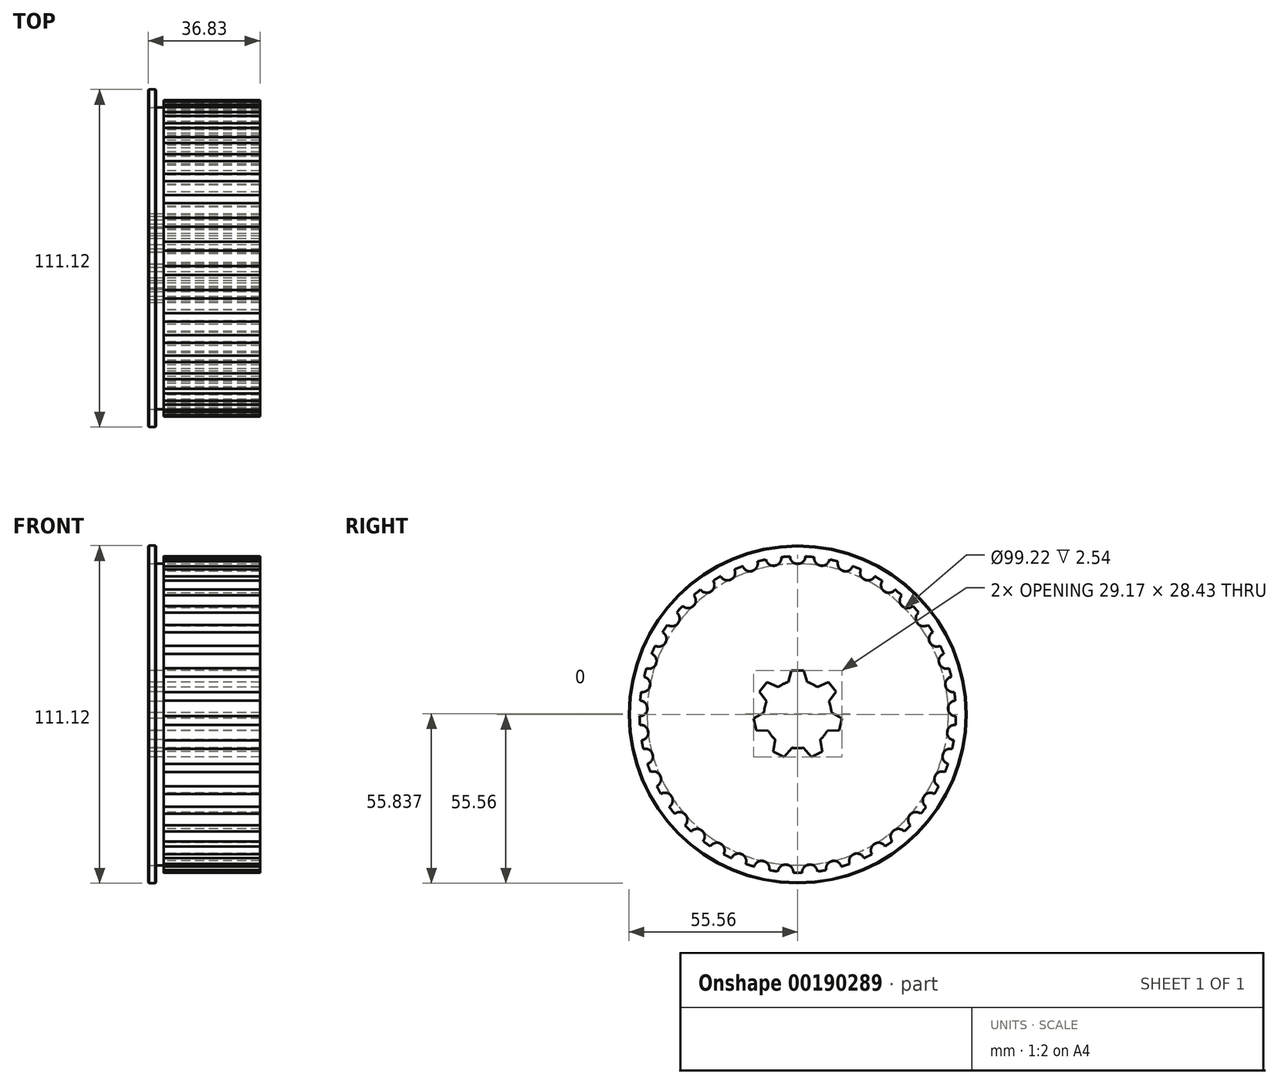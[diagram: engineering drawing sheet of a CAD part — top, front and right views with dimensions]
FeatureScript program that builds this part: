
annotation { "Feature Type Name" : "Feature", "Feature Type Description" : "" }
export const myFeature = defineFeature(function(context is Context, id is Id, definition is map)
    precondition{}
    {
        {
            var Q0;
            Q0=qCreatedBy(makeId("Right.planeOp"),FACE);
            var sketch = newSketch(context, id + "F9", { "sketchPlane" : qUnion([Q0])});
            skArc(sketch, "E0", {"start": v(-2.54, 52) * mm, "mid": v(0, -52.07) * mm, "end": v(2.54, 52) * mm});
            skArc(sketch, "E1", {"start": v(-2.54, 52) * mm, "mid": v(0, 49.53) * mm, "end": v(2.54, 52) * mm});
            skArc(sketch, "E2.1.0", {"start": v(-10.45, 51.01) * mm, "mid": v(-7.56, 48.95) * mm, "end": v(-5.43, 51.79) * mm});
            skArc(sketch, "E2.2.0", {"start": v(-18.11, 48.82) * mm, "mid": v(-14.94, 47.22) * mm, "end": v(-13.27, 50.35) * mm});
            skArc(sketch, "E2.3.0", {"start": v(-25.35, 45.48) * mm, "mid": v(-21.98, 44.39) * mm, "end": v(-20.8, 47.73) * mm});
            skArc(sketch, "E2.4.0", {"start": v(-32, 41.08) * mm, "mid": v(-28.5, 40.51) * mm, "end": v(-27.84, 44) * mm});
            skArc(sketch, "E2.5.0", {"start": v(-37.9, 35.71) * mm, "mid": v(-34.35, 35.69) * mm, "end": v(-34.23, 39.23) * mm});
            skArc(sketch, "E2.6.0", {"start": v(-42.9, 29.5) * mm, "mid": v(-39.4, 30.03) * mm, "end": v(-39.82, 33.55) * mm});
            skArc(sketch, "E2.7.0", {"start": v(-46.9, 22.61) * mm, "mid": v(-43.51, 23.66) * mm, "end": v(-44.48, 27.08) * mm});
            skArc(sketch, "E2.8.0", {"start": v(-49.8, 15.19) * mm, "mid": v(-46.61, 16.74) * mm, "end": v(-48.09, 19.97) * mm});
            skArc(sketch, "E2.9.0", {"start": v(-51.54, 7.4) * mm, "mid": v(-48.62, 9.43) * mm, "end": v(-50.57, 12.4) * mm});
            skArc(sketch, "E2.10.0", {"start": v(-52.07, -0.55) * mm, "mid": v(-49.5, 1.9) * mm, "end": v(-51.87, 4.53) * mm});
            skArc(sketch, "E2.11.0", {"start": v(-51.37, -8.49) * mm, "mid": v(-49.2, -5.68) * mm, "end": v(-51.96, -3.44) * mm});
            skArc(sketch, "E2.12.0", {"start": v(-49.48, -16.23) * mm, "mid": v(-47.76, -13.12) * mm, "end": v(-50.82, -11.33) * mm});
            skArc(sketch, "E2.13.0", {"start": v(-46.42, -23.6) * mm, "mid": v(-45.2, -20.26) * mm, "end": v(-48.5, -18.96) * mm});
            skArc(sketch, "E2.14.0", {"start": v(-42.27, -30.4) * mm, "mid": v(-41.57, -26.92) * mm, "end": v(-45.03, -26.14) * mm});
            skArc(sketch, "E2.15.0", {"start": v(-37.14, -36.5) * mm, "mid": v(-36.98, -32.95) * mm, "end": v(-40.52, -32.7) * mm});
            skArc(sketch, "E2.16.0", {"start": v(-31.13, -41.74) * mm, "mid": v(-31.51, -38.21) * mm, "end": v(-35.05, -38.5) * mm});
            skArc(sketch, "E2.17.0", {"start": v(-24.4, -46) * mm, "mid": v(-25.31, -42.57) * mm, "end": v(-28.76, -43.4) * mm});
            skArc(sketch, "E2.18.0", {"start": v(-17.09, -49.19) * mm, "mid": v(-18.52, -45.94) * mm, "end": v(-21.8, -47.29) * mm});
            skArc(sketch, "E2.19.0", {"start": v(-9.38, -51.22) * mm, "mid": v(-11.29, -48.23) * mm, "end": v(-14.32, -50.06) * mm});
            skArc(sketch, "E2.20.0", {"start": v(-1.45, -52.05) * mm, "mid": v(-3.8, -49.38) * mm, "end": v(-6.51, -51.66) * mm});
            skArc(sketch, "E2.21.0", {"start": v(6.51, -51.66) * mm, "mid": v(3.8, -49.38) * mm, "end": v(1.45, -52.05) * mm});
            skArc(sketch, "E2.22.0", {"start": v(14.32, -50.06) * mm, "mid": v(11.29, -48.23) * mm, "end": v(9.38, -51.22) * mm});
            skArc(sketch, "E2.23.0", {"start": v(21.8, -47.29) * mm, "mid": v(18.52, -45.94) * mm, "end": v(17.09, -49.19) * mm});
            skArc(sketch, "E2.24.0", {"start": v(28.76, -43.4) * mm, "mid": v(25.31, -42.57) * mm, "end": v(24.4, -46) * mm});
            skArc(sketch, "E2.25.0", {"start": v(35.05, -38.5) * mm, "mid": v(31.51, -38.21) * mm, "end": v(31.13, -41.74) * mm});
            skArc(sketch, "E2.26.0", {"start": v(40.52, -32.7) * mm, "mid": v(36.98, -32.95) * mm, "end": v(37.14, -36.5) * mm});
            skArc(sketch, "E2.27.0", {"start": v(45.03, -26.14) * mm, "mid": v(41.57, -26.92) * mm, "end": v(42.27, -30.4) * mm});
            skArc(sketch, "E2.28.0", {"start": v(48.5, -18.96) * mm, "mid": v(45.2, -20.26) * mm, "end": v(46.42, -23.6) * mm});
            skArc(sketch, "E2.29.0", {"start": v(50.82, -11.33) * mm, "mid": v(47.76, -13.12) * mm, "end": v(49.48, -16.23) * mm});
            skArc(sketch, "E2.30.0", {"start": v(51.96, -3.44) * mm, "mid": v(49.2, -5.68) * mm, "end": v(51.37, -8.49) * mm});
            skArc(sketch, "E2.31.0", {"start": v(51.87, 4.53) * mm, "mid": v(49.5, 1.9) * mm, "end": v(52.07, -0.55) * mm});
            skArc(sketch, "E2.32.0", {"start": v(50.57, 12.4) * mm, "mid": v(48.62, 9.43) * mm, "end": v(51.54, 7.4) * mm});
            skArc(sketch, "E2.33.0", {"start": v(48.09, 19.97) * mm, "mid": v(46.61, 16.74) * mm, "end": v(49.8, 15.19) * mm});
            skArc(sketch, "E2.34.0", {"start": v(44.48, 27.08) * mm, "mid": v(43.51, 23.66) * mm, "end": v(46.9, 22.61) * mm});
            skArc(sketch, "E2.35.0", {"start": v(39.82, 33.55) * mm, "mid": v(39.4, 30.03) * mm, "end": v(42.9, 29.5) * mm});
            skArc(sketch, "E2.36.0", {"start": v(34.23, 39.23) * mm, "mid": v(34.35, 35.69) * mm, "end": v(37.9, 35.71) * mm});
            skArc(sketch, "E2.37.0", {"start": v(27.84, 44) * mm, "mid": v(28.5, 40.51) * mm, "end": v(32, 41.08) * mm});
            skArc(sketch, "E2.38.0", {"start": v(20.8, 47.73) * mm, "mid": v(21.98, 44.39) * mm, "end": v(25.35, 45.48) * mm});
            skArc(sketch, "E2.39.0", {"start": v(13.27, 50.35) * mm, "mid": v(14.94, 47.22) * mm, "end": v(18.11, 48.82) * mm});
            skArc(sketch, "E2.40.0", {"start": v(5.43, 51.79) * mm, "mid": v(7.56, 48.95) * mm, "end": v(10.45, 51.01) * mm});
            skSolve(sketch);
        }
        {
            var Q0;
            {var subQ3=sQuery(id+"F9.wireOp",EDGE,"E1");Q0=makeQuery(id+"F9.imprint","IMPRINT",FACE,{"disambiguationData":[TD([[makeQuery(id+"F9.imprint","IMPRINT",EDGE,{"derivedFrom":subQ3}),-1.0]])]});}
            var sketch = newSketch(context, id + "F10", { "sketchPlane" : qUnion([Q0])});
            skSolve(sketch);
        }
        {
            var Q0;
            Q0 = qSketchRegion(id + "F10", true);
            var Q1;
            {var subQ3=sQuery(id+"F9.wireOp",EDGE,"E1");Q1=makeQuery(id+"F9.imprint","IMPRINT",FACE,{"disambiguationData":[TD([[makeQuery(id+"F9.imprint","IMPRINT",EDGE,{"derivedFrom":subQ3}),-1.0]])]});}
            extrude(context, id + "F0", {"entities" : qUnion([Q0, Q1]), "depth" : 31.75 * mm});
        }
        {
            var Q0;
            Q0=qCreatedBy(makeId("Right.planeOp"),FACE);
            var sketch = newSketch(context, id + "F1", { "sketchPlane" : qUnion([Q0])});
            skCircle(sketch, "E3", {"center": v(0, 0) * mm, "radius": 49.61 * mm});
            skSolve(sketch);
        }
        {
            var Q0;
            Q0 = qSketchRegion(id + "F1", true);
            extrude(context, id + "F2", {"entities" : qUnion([Q0]), "operationType" : NewBodyOperationType.ADD, "oppositeDirection" : true, "depth" : 2.54 * mm});
        }
        {
            var Q0;
            Q0=makeQuery(id+"F2.opExtrude","CAP_FACE",FACE,{"disambiguationData":[OSD([sQuery(id+"F1.wireOp",EDGE,"E3")])],"isStart":false});
            var sketch = newSketch(context, id + "F3", { "sketchPlane" : qUnion([Q0])});
            skCircle(sketch, "E4", {"center": v(0, 0) * mm, "radius": 55.56 * mm});
            skSolve(sketch);
        }
        {
            var Q0;
            Q0=makeQuery(id+"F3.imprint","IMPRINT",FACE,{"disambiguationData":[TD([[makeQuery(id+"F3.imprint","IMPRINT",EDGE,{"derivedFrom":sQuery(id+"F3.wireOp",EDGE,"E4")}),1.0]])]});
            extrude(context, id + "F4", {"entities" : qUnion([Q0]), "depth" : 2.54 * mm});
        }
        {
            var Q0;
            Q0=makeQuery(id+"F2.opExtrude","CAP_FACE",FACE,{"disambiguationData":[OSD([sQuery(id+"F1.wireOp",EDGE,"E3")])],"isStart":false});
            extrude(context, id + "F5", {"entities" : qUnion([Q0]), "depth" : 2.54 * mm});
        }
        {
            var Q0;
            Q0=makeQuery(id+"F4.opExtrude","CAP_EDGE",EDGE,{"disambiguationData":[OSD([sQuery(id+"F3.wireOp",EDGE,"E4")])],"isStart":true});
            var Q1;
            Q1=makeQuery(id+"F4.opExtrude","CAP_EDGE",EDGE,{"disambiguationData":[OSD([sQuery(id+"F3.wireOp",EDGE,"E4")])],"isStart":false});
            chamfer(context, id + "F6", {"entities" : qUnion([Q0, Q1]), "width" : 0.25 * mm, "tangentPropagation" : true});
        }
        {
            var Q0;
            Q0=makeQuery(id+"F5.opExtrude","CAP_FACE",FACE,{"disambiguationData":[OSD([sQuery(id+"F1.wireOp",EDGE,"E3")])],"isStart":false});
            var sketch = newSketch(context, id + "F7", { "sketchPlane" : qUnion([Q0])});
            skArc(sketch, "E5", {"start": v(-3.06, 10.68) * mm, "mid": v(-4.82, 10.01) * mm, "end": v(-6.45, 9.05) * mm});
            skPoint(sketch, "E6", {"position": v(-3.06, 10.68) * mm});
            skPoint(sketch, "E7", {"position": v(3.06, 10.68) * mm});
            skPoint(sketch, "E8", {"position": v(0, 14.5) * mm});
            skPoint(sketch, "E9", {"position": v(-2.03, 14.5) * mm});
            skPoint(sketch, "E10", {"position": v(2.03, 14.5) * mm});
            skLineSegment(sketch, "E11", {"start": v(-3.06, 10.68) * mm, "end": v(-2.03, 14.5) * mm});
            skLineSegment(sketch, "E12", {"start": v(2.03, 14.5) * mm, "end": v(-2.03, 14.5) * mm});
            skLineSegment(sketch, "E13", {"start": v(3.06, 10.68) * mm, "end": v(2.03, 14.5) * mm});
            skLineSegment(sketch, "E14.1.0", {"start": v(-10.26, 4.27) * mm, "end": v(-12.6, 7.45) * mm});
            skPoint(sketch, "E14.1.1", {"position": v(-11.33, 9.04) * mm});
            skPoint(sketch, "E14.1.2", {"position": v(-12.6, 7.45) * mm});
            skPoint(sketch, "E14.1.3", {"position": v(-10.07, 10.63) * mm});
            skLineSegment(sketch, "E14.1.4", {"start": v(-10.07, 10.63) * mm, "end": v(-12.6, 7.45) * mm});
            skLineSegment(sketch, "E14.1.5", {"start": v(-6.45, 9.05) * mm, "end": v(-10.07, 10.63) * mm});
            skLineSegment(sketch, "E14.2.0", {"start": v(-9.74, -5.36) * mm, "end": v(-13.68, -5.2) * mm});
            skPoint(sketch, "E14.2.1", {"position": v(-14.13, -3.23) * mm});
            skPoint(sketch, "E14.2.2", {"position": v(-13.68, -5.2) * mm});
            skPoint(sketch, "E14.2.3", {"position": v(-14.58, -1.24) * mm});
            skLineSegment(sketch, "E14.2.4", {"start": v(-14.58, -1.24) * mm, "end": v(-13.68, -5.2) * mm});
            skLineSegment(sketch, "E14.2.5", {"start": v(-11.1, 0.6) * mm, "end": v(-14.58, -1.24) * mm});
            skLineSegment(sketch, "E14.3.0", {"start": v(-1.88, -10.95) * mm, "end": v(-4.46, -13.94) * mm});
            skPoint(sketch, "E14.3.1", {"position": v(-6.29, -13.06) * mm});
            skPoint(sketch, "E14.3.2", {"position": v(-4.46, -13.94) * mm});
            skPoint(sketch, "E14.3.3", {"position": v(-8.12, -12.18) * mm});
            skLineSegment(sketch, "E14.3.4", {"start": v(-8.12, -12.18) * mm, "end": v(-4.46, -13.94) * mm});
            skLineSegment(sketch, "E14.3.5", {"start": v(-7.39, -8.3) * mm, "end": v(-8.12, -12.18) * mm});
            skLineSegment(sketch, "E14.4.0", {"start": v(7.39, -8.3) * mm, "end": v(8.12, -12.18) * mm});
            skPoint(sketch, "E14.4.1", {"position": v(6.29, -13.06) * mm});
            skPoint(sketch, "E14.4.2", {"position": v(8.12, -12.18) * mm});
            skPoint(sketch, "E14.4.3", {"position": v(4.46, -13.94) * mm});
            skLineSegment(sketch, "E14.4.4", {"start": v(4.46, -13.94) * mm, "end": v(8.12, -12.18) * mm});
            skLineSegment(sketch, "E14.4.5", {"start": v(1.88, -10.95) * mm, "end": v(4.46, -13.94) * mm});
            skLineSegment(sketch, "E14.5.0", {"start": v(11.1, 0.6) * mm, "end": v(14.58, -1.24) * mm});
            skPoint(sketch, "E14.5.1", {"position": v(14.13, -3.23) * mm});
            skPoint(sketch, "E14.5.2", {"position": v(14.58, -1.24) * mm});
            skPoint(sketch, "E14.5.3", {"position": v(13.68, -5.2) * mm});
            skLineSegment(sketch, "E14.5.4", {"start": v(13.68, -5.2) * mm, "end": v(14.58, -1.24) * mm});
            skLineSegment(sketch, "E14.5.5", {"start": v(9.74, -5.36) * mm, "end": v(13.68, -5.2) * mm});
            skLineSegment(sketch, "E14.6.0", {"start": v(6.45, 9.05) * mm, "end": v(10.07, 10.63) * mm});
            skPoint(sketch, "E14.6.1", {"position": v(11.33, 9.04) * mm});
            skPoint(sketch, "E14.6.2", {"position": v(10.07, 10.63) * mm});
            skPoint(sketch, "E14.6.3", {"position": v(12.6, 7.45) * mm});
            skLineSegment(sketch, "E14.6.4", {"start": v(12.6, 7.45) * mm, "end": v(10.07, 10.63) * mm});
            skLineSegment(sketch, "E14.6.5", {"start": v(10.26, 4.27) * mm, "end": v(12.6, 7.45) * mm});
            skArc(sketch, "E15.trimOffspring", {"start": v(-10.26, 4.27) * mm, "mid": v(-10.83, 2.47) * mm, "end": v(-11.1, 0.6) * mm});
            skArc(sketch, "E16.trimOffspring", {"start": v(-9.74, -5.36) * mm, "mid": v(-8.69, -6.93) * mm, "end": v(-7.39, -8.3) * mm});
            skArc(sketch, "E17.trimOffspring", {"start": v(-1.88, -10.95) * mm, "mid": v(0, -11.11) * mm, "end": v(1.88, -10.95) * mm});
            skArc(sketch, "E18.trimOffspring", {"start": v(7.39, -8.3) * mm, "mid": v(8.69, -6.93) * mm, "end": v(9.74, -5.36) * mm});
            skArc(sketch, "E19.trimOffspring", {"start": v(11.1, 0.6) * mm, "mid": v(10.83, 2.47) * mm, "end": v(10.26, 4.27) * mm});
            skArc(sketch, "E20.trimOffspring", {"start": v(6.45, 9.05) * mm, "mid": v(4.82, 10.01) * mm, "end": v(3.06, 10.68) * mm});
            skSolve(sketch);
        }
        {
            var Q0;
            Q0=makeQuery(id+"F7.imprint","IMPRINT",FACE,{"disambiguationData":[TD([[makeQuery(id+"F7.imprint","IMPRINT",EDGE,{"derivedFrom":sQuery(id+"F7.wireOp",EDGE,"E5")}),1.0]])]});
            extrude(context, id + "F8", {"entities" : qUnion([Q0]), "operationType" : NewBodyOperationType.REMOVE, "endBound" : BoundingType.THROUGH_ALL, "oppositeDirection" : true, "depth" : 63.5 * mm});
        }
    });
